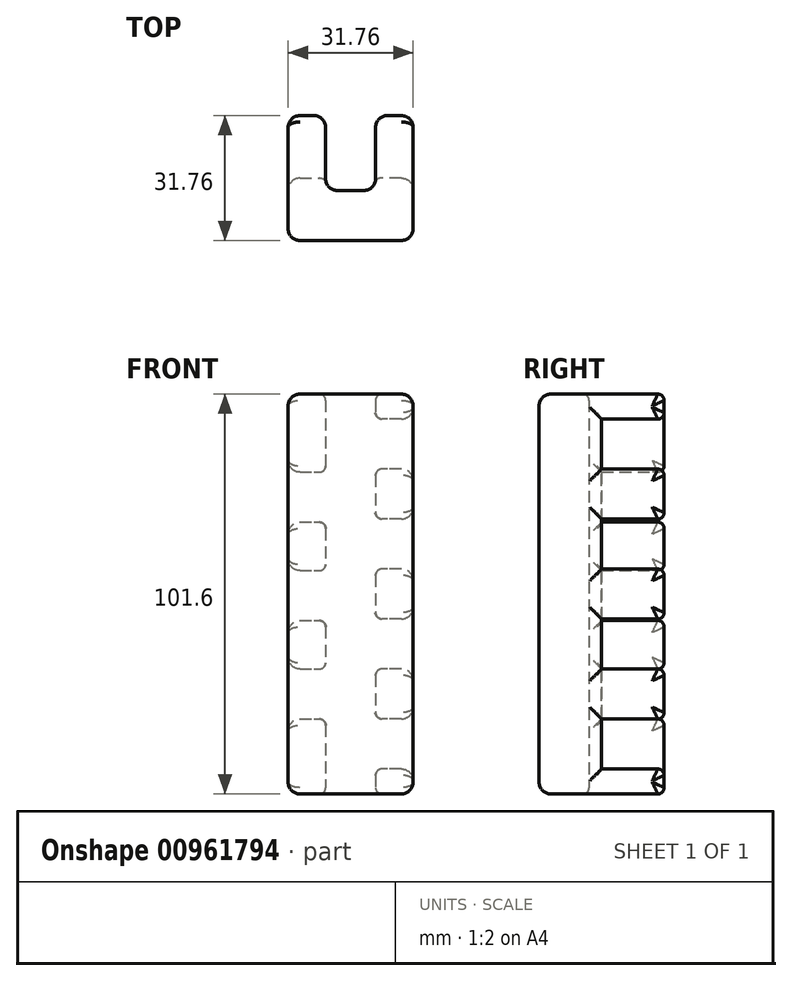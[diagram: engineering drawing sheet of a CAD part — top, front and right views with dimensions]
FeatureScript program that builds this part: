
annotation { "Feature Type Name" : "Feature", "Feature Type Description" : "" }
export const myFeature = defineFeature(function(context is Context, id is Id, definition is map)
    precondition{}
    {
        {
            var Q0;
            Q0=qCreatedBy(makeId("Top.planeOp"),FACE);
            var sketch = newSketch(context, id + "F0", { "sketchPlane" : qUnion([Q0])});
            skLineSegment(sketch, "E0.bottom", {"start": v(15.88, -15.87) * mm, "end": v(-15.87, -15.88) * mm});
            skLineSegment(sketch, "E0.top", {"start": v(15.88, 15.88) * mm, "end": v(-15.87, 15.88) * mm});
            skLineSegment(sketch, "E0.left", {"start": v(15.88, -15.88) * mm, "end": v(15.88, 15.88) * mm});
            skLineSegment(sketch, "E0.right", {"start": v(-15.87, -15.88) * mm, "end": v(-15.87, 15.88) * mm});
            skPoint(sketch, "E0.middle", {"position": v(0, 0) * mm});
            skPoint(sketch, "E1", {"position": v(-6.35, 15.87) * mm});
            skPoint(sketch, "E2", {"position": v(0, 15.88) * mm});
            skLineSegment(sketch, "E3.bottom", {"start": v(-6.35, 15.87) * mm, "end": v(6.35, 15.87) * mm});
            skLineSegment(sketch, "E3.top", {"start": v(-6.35, -3.18) * mm, "end": v(6.35, -3.18) * mm});
            skLineSegment(sketch, "E3.left", {"start": v(-6.35, 15.87) * mm, "end": v(-6.35, -3.18) * mm});
            skLineSegment(sketch, "E3.right", {"start": v(6.35, 15.88) * mm, "end": v(6.35, -3.18) * mm});
            skSolve(sketch);
        }
        {
            var Q0;
            Q0=makeQuery(id+"F0.imprint","IMPRINT",FACE,{"disambiguationData":[TD([[makeQuery(id+"F0.imprint","IMPRINT",EDGE,{"derivedFrom":sQuery(id+"F0.wireOp",EDGE,"E0.bottom")}),-1.0]])]});
            extrude(context, id + "F1", {"entities" : qUnion([Q0]), "depth" : 101.6 * mm, "offsetDistance" : 25 * mm});
        }
        {
            var Q0;
            Q0=makeQuery(id+"F1.opExtrude","SWEPT_EDGE",EDGE,{"disambiguationData":[OSD([sQuery(id+"F0.wireOp",EDGE,"E0.top"),sQuery(id+"F0.wireOp",EDGE,"E3.bottom"),sQuery(id+"F0.wireOp",EDGE,"E3.right")])]});
            var Q1;
            Q1=makeQuery(id+"F1.opExtrude","SWEPT_EDGE",EDGE,{"disambiguationData":[OSD([sQuery(id+"F0.wireOp",EDGE,"E0.top"),sQuery(id+"F0.wireOp",EDGE,"E3.bottom"),sQuery(id+"F0.wireOp",EDGE,"E3.left")])]});
            var Q2;
            Q2=makeQuery(id+"F1.opExtrude","SWEPT_EDGE",EDGE,{"disambiguationData":[OSD([sQuery(id+"F0.wireOp",EDGE,"E3.top"),sQuery(id+"F0.wireOp",EDGE,"E3.left")])]});
            var Q3;
            Q3=makeQuery(id+"F1.opExtrude","SWEPT_EDGE",EDGE,{"disambiguationData":[OSD([sQuery(id+"F0.wireOp",EDGE,"E3.top"),sQuery(id+"F0.wireOp",EDGE,"E3.right")])]});
            fillet(context, id + "F2", {"entities" : qUnion([Q0, Q1, Q2, Q3]), "radius" : 3 * mm, "tangentPropagation" : true, "allowEdgeOverflow" : false});
        }
        {
            var Q0;
            Q0=qCreatedBy(makeId("Right.planeOp"),FACE);
            var sketch = newSketch(context, id + "F3", { "sketchPlane" : qUnion([Q0])});
            skLineSegment(sketch, "E4.bottom", {"start": v(0, 6.35) * mm, "end": v(15.88, 6.35) * mm});
            skLineSegment(sketch, "E4.top", {"start": v(0, 19.05) * mm, "end": v(15.88, 19.05) * mm});
            skLineSegment(sketch, "E4.left", {"start": v(0, 6.35) * mm, "end": v(0, 19.05) * mm});
            skLineSegment(sketch, "E4.right", {"start": v(15.88, 6.35) * mm, "end": v(15.88, 19.05) * mm});
            skLineSegment(sketch, "E5.0.1.0", {"start": v(0, 44.45) * mm, "end": v(15.88, 44.45) * mm});
            skLineSegment(sketch, "E5.0.1.1", {"start": v(15.88, 31.75) * mm, "end": v(15.88, 44.45) * mm});
            skLineSegment(sketch, "E5.0.1.2", {"start": v(0, 31.75) * mm, "end": v(15.88, 31.75) * mm});
            skLineSegment(sketch, "E5.0.1.3", {"start": v(0, 31.75) * mm, "end": v(0, 44.45) * mm});
            skLineSegment(sketch, "E5.0.2.0", {"start": v(0, 69.85) * mm, "end": v(15.88, 69.85) * mm});
            skLineSegment(sketch, "E5.0.2.1", {"start": v(15.88, 57.15) * mm, "end": v(15.88, 69.85) * mm});
            skLineSegment(sketch, "E5.0.2.2", {"start": v(0, 57.15) * mm, "end": v(15.88, 57.15) * mm});
            skLineSegment(sketch, "E5.0.2.3", {"start": v(0, 57.15) * mm, "end": v(0, 69.85) * mm});
            skLineSegment(sketch, "E5.0.3.0", {"start": v(0, 95.25) * mm, "end": v(15.88, 95.25) * mm});
            skLineSegment(sketch, "E5.0.3.1", {"start": v(15.88, 82.55) * mm, "end": v(15.88, 95.25) * mm});
            skLineSegment(sketch, "E5.0.3.2", {"start": v(0, 82.55) * mm, "end": v(15.88, 82.55) * mm});
            skLineSegment(sketch, "E5.0.3.3", {"start": v(0, 82.55) * mm, "end": v(0, 95.25) * mm});
            skLineSegment(sketch, "E5.direction1", {"start": v(0, 12.7) * mm, "end": v(25, 12.7) * mm, "construction": true});
            skLineSegment(sketch, "E5.direction2", {"start": v(0, 12.7) * mm, "end": v(0, 38.1) * mm, "construction": true});
            skSolve(sketch);
        }
        {
            var Q0;
            Q0 = qSketchRegion(id + "F3", true);
            var Q1;
            Q1=makeQuery(id+"F1.opExtrude","SWEPT_FACE",FACE,{"disambiguationData":[OSD([sQuery(id+"F0.wireOp",EDGE,"E0.left")])]});
            extrude(context, id + "F4", {"entities" : qUnion([Q0]), "operationType" : NewBodyOperationType.REMOVE, "endBound" : BoundingType.UP_TO_SURFACE, "depth" : 25 * mm, "endBoundEntityFace" : qUnion([Q1]), "offsetDistance" : 25 * mm});
        }
        {
            var Q0;
            Q0=qCreatedBy(makeId("Right.planeOp"),FACE);
            var sketch = newSketch(context, id + "F5", { "sketchPlane" : qUnion([Q0])});
            skLineSegment(sketch, "E6.bottom", {"start": v(0, 19.05) * mm, "end": v(15.88, 19.05) * mm});
            skLineSegment(sketch, "E6.top", {"start": v(0, 31.75) * mm, "end": v(15.88, 31.75) * mm});
            skLineSegment(sketch, "E6.left", {"start": v(0, 19.05) * mm, "end": v(0, 31.75) * mm});
            skLineSegment(sketch, "E6.right", {"start": v(15.88, 19.05) * mm, "end": v(15.88, 31.75) * mm});
            skLineSegment(sketch, "E7.0.1.0", {"start": v(0, 56.75) * mm, "end": v(15.88, 56.75) * mm});
            skLineSegment(sketch, "E7.0.1.1", {"start": v(0, 44.05) * mm, "end": v(0, 56.75) * mm});
            skLineSegment(sketch, "E7.0.1.2", {"start": v(0, 44.05) * mm, "end": v(15.88, 44.05) * mm});
            skLineSegment(sketch, "E7.0.1.3", {"start": v(15.88, 44.05) * mm, "end": v(15.88, 56.75) * mm});
            skLineSegment(sketch, "E7.0.2.0", {"start": v(0, 81.75) * mm, "end": v(15.88, 81.75) * mm});
            skLineSegment(sketch, "E7.0.2.1", {"start": v(0, 69.05) * mm, "end": v(0, 81.75) * mm});
            skLineSegment(sketch, "E7.0.2.2", {"start": v(0, 69.05) * mm, "end": v(15.88, 69.05) * mm});
            skLineSegment(sketch, "E7.0.2.3", {"start": v(15.88, 69.05) * mm, "end": v(15.88, 81.75) * mm});
            skLineSegment(sketch, "E7.direction1", {"start": v(0, 31.75) * mm, "end": v(25, 31.75) * mm, "construction": true});
            skLineSegment(sketch, "E7.direction2", {"start": v(0, 31.75) * mm, "end": v(0, 56.75) * mm, "construction": true});
            skSolve(sketch);
        }
        {
            var Q0;
            Q0 = qSketchRegion(id + "F5", true);
            var Q1;
            Q1=makeQuery(id+"F1.opExtrude","SWEPT_FACE",FACE,{"disambiguationData":[OSD([sQuery(id+"F0.wireOp",EDGE,"E0.right")])]});
            extrude(context, id + "F6", {"entities" : qUnion([Q0]), "operationType" : NewBodyOperationType.REMOVE, "endBound" : BoundingType.UP_TO_SURFACE, "oppositeDirection" : true, "depth" : 25 * mm, "endBoundEntityFace" : qUnion([Q1]), "offsetDistance" : 25 * mm});
        }
        {
            var Q0;
            Q0=makeQuery(id+"F1.opExtrude","SWEPT_FACE",FACE,{"disambiguationData":[OSD([sQuery(id+"F0.wireOp",EDGE,"E3.left")])]});
            var Q1;
            Q1=makeQuery(id+"F1.opExtrude","SWEPT_FACE",FACE,{"disambiguationData":[OSD([sQuery(id+"F0.wireOp",EDGE,"E3.right")])]});
            fillet(context, id + "F7", {"entities" : qUnion([Q0, Q1]), "radius" : 1.6 * mm, "tangentPropagation" : true, "allowEdgeOverflow" : false});
        }
        {
            var Q0;
            Q0=makeQuery(id+"F1.opExtrude","CAP_EDGE",EDGE,{"disambiguationData":[OSD([sQuery(id+"F0.wireOp",EDGE,"E0.right")])],"isStart":false});
            var Q1;
            Q1=makeQuery(id+"F1.opExtrude","CAP_EDGE",EDGE,{"disambiguationData":[OSD([sQuery(id+"F0.wireOp",EDGE,"E0.bottom")])],"isStart":false});
            var Q2;
            Q2=makeQuery(id+"F1.opExtrude","CAP_EDGE",EDGE,{"disambiguationData":[OSD([sQuery(id+"F0.wireOp",EDGE,"E0.left")])],"isStart":false});
            var Q3;
            Q3=makeQuery(id+"F1.opExtrude","SWEPT_EDGE",EDGE,{"disambiguationData":[OSD([sQuery(id+"F0.wireOp",EDGE,"E0.bottom"),sQuery(id+"F0.wireOp",EDGE,"E0.left")])]});
            var Q4;
            Q4=makeQuery(id+"F1.opExtrude","SWEPT_EDGE",EDGE,{"disambiguationData":[OSD([sQuery(id+"F0.wireOp",EDGE,"E0.bottom"),sQuery(id+"F0.wireOp",EDGE,"E0.right")])]});
            var Q5;
            Q5=makeQuery(id+"F1.opExtrude","CAP_EDGE",EDGE,{"disambiguationData":[OSD([sQuery(id+"F0.wireOp",EDGE,"E0.bottom")])],"isStart":true});
            var Q6;
            Q6=makeQuery(id+"F1.opExtrude","CAP_EDGE",EDGE,{"disambiguationData":[OSD([sQuery(id+"F0.wireOp",EDGE,"E0.left")])],"isStart":true});
            var Q7;
            Q7=makeQuery(id+"F1.opExtrude","CAP_EDGE",EDGE,{"disambiguationData":[OSD([sQuery(id+"F0.wireOp",EDGE,"E0.right")])],"isStart":true});
            fillet(context, id + "F8", {"entities" : qUnion([Q0, Q1, Q2, Q3, Q4, Q5, Q6, Q7]), "radius" : 3 * mm, "tangentPropagation" : true, "allowEdgeOverflow" : false});
        }
        {
            var Q0;
            Q0=makeQuery(id+"F1.opExtrude","SWEPT_FACE",FACE,{"disambiguationData":[OSD([sQuery(id+"F0.wireOp",EDGE,"E0.left")])]});
            var Q1;
            Q1=makeQuery(id+"F1.opExtrude","SWEPT_FACE",FACE,{"disambiguationData":[OSD([sQuery(id+"F0.wireOp",EDGE,"E0.right")])]});
            fillet(context, id + "F9", {"entities" : qUnion([Q0, Q1]), "radius" : 3 * mm, "tangentPropagation" : true, "allowEdgeOverflow" : false});
        }
    });
